# Revit family: Storage-Teknion-CWSC_Credenza_Closed_Cabinet-R2020
name_source: partatom
category: Furniture
units: mm (PartAtom-declared; Revit-internal decimal feet)

## family parameters
Always vertical = Yes
Cut with Voids When Loaded = No
OmniClass Number = 23.40.20.00
OmniClass Title = General Furniture and Specialties
Room Calculation Point = No
Shared = Yes
Work Plane-Based = No

## types (4) — shared parameters
Assembly Code = E2020200
Case, Back & Front Finish = Laminate - Teknion - RV - Very White
Manufacturer = Teknion
Manufacturer Fax = 416.661.4586
Model = CWSC____
Part Number = CWSC
Product Documentation Link = https://assets.teknion.com
Product Line = C+D
Product Page URL = https://www.teknion.com
Pull Finish = Paint - Teknion - Mica - Graphite
Series = Custom Wood
Sustainability Data = https://www.teknion.com
URL = www.teknion.com
Unit Weight URL = http://www.teknion.com
Warranty = http://www.teknion.com
zero-valued in all types: Default Elevation

## per-type parameters (varying)
| type | Description | Glass Top Visibility | Solid Top Visibility | Top Finish | Top Finish Note |
| Has White Solid Surface | Custom Wood Credenza, 1/2" Top, Closed Cabinet, White Solid Surface Top | No | Yes | Wood - Teknion - MV - Solid Surface - Glacier White | Choose Glacier White below |
| Has Grey Solid Surface Top | Custom Wood Credenza, 1/2" Top, Closed Cabinet, Grey Solid Surface Top | No | Yes | Wood - Teknion - MM - Solid Surface - Elegant Grey | Choose either a Silver Grey or Elegant Grey finish below |
| Has Backpainted Glass Top | Custom Wood Credenza, 1/2" Top, Closed Cabinet, Backpainted Glass Top | Yes | No | Back-painted Glass - K1 - Teknion - Storm White | Choose a Backpainted glass finish below |
| Has Veneer Top | Custom Wood Credenza, 1/2" Top, Closed Cabinet, Veneer Top | No | Yes | Wood - Teknion - DV - Sierra (Horizontal Grain) | Choose a Veneer Finish below |

## geometry (parser evidence)
native form markers: Blend x43, Sweep x1
no freeform markers — native parametric forms only
